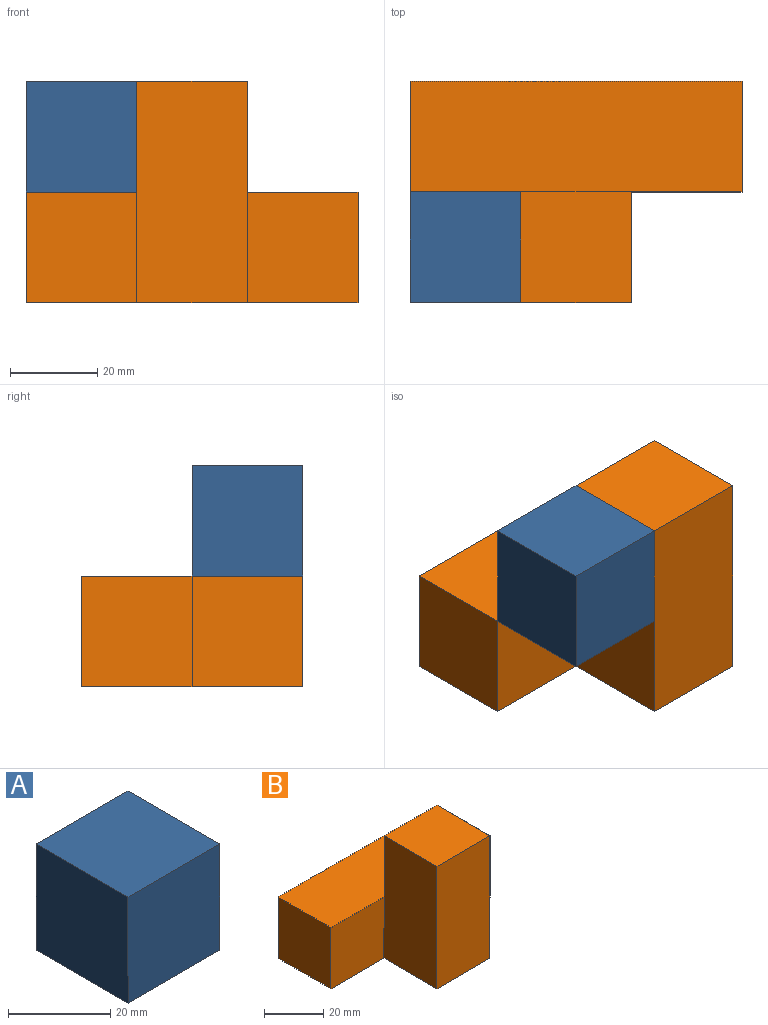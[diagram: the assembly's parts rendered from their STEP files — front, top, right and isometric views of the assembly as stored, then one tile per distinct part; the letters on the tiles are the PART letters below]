
ASSEMBLY  parts=2 mates=1
PART A: 6 faces, bbox 25.4x25.4x25.4 mm
  f0: plane 25.4x25.4mm, normal (-1,0,0), area 645.2mm2, adj f1,f3,f4,f5
  f1: plane 25.4x25.4mm, normal (0,0,-1), area 645.2mm2, adj f0,f2,f4,f5
  f2: plane 25.4x25.4mm, normal (1,0,0), area 645.2mm2, adj f1,f3,f4,f5
  f3: plane 25.4x25.4mm, normal (0,0,1), area 645.2mm2, adj f0,f2,f4,f5
  f4: plane 25.4x25.4mm, normal (0,-1,0), area 645.2mm2, adj f0,f1,f2,f3
  f5: plane 25.4x25.4mm, normal (0,1,0), area 645.2mm2, adj f0,f1,f2,f3
PART B: 12 faces, bbox 76.2x50.8x50.8 mm
  f0: plane 76.2x25.4mm, normal (0,0,1), area 1935.5mm2, adj f1,f2,f4,f5,f6,f10
  f1: plane 25.4x25.4mm, normal (0,-1,0), area 645.2mm2, adj f0,f3,f6,f7
  f2: plane 25.4x25.4mm, normal (0,-1,0), area 645.2mm2, adj f0,f3,f5,f8
  f3: plane 76.2x50.8mm, normal (0,0,-1), area 2580.6mm2, adj f1,f2,f4,f5,f6,f7,f8,f9
  f4: plane 76.2x25.4mm, normal (0,1,0), area 1935.5mm2, adj f0,f3,f5,f6
  f5: plane 25.4x25.4mm, normal (1,0,0), area 645.2mm2, adj f0,f2,f3,f4
  f6: plane 25.4x25.4mm, normal (-1,0,0), area 645.2mm2, adj f0,f1,f3,f4
  f7: plane 50.8x25.4mm, normal (-1,0,0), area 1290.3mm2, adj f1,f3,f9,f10,f11
  f8: plane 50.8x25.4mm, normal (1,0,0), area 1290.3mm2, adj f2,f3,f9,f10,f11
  f9: plane 50.8x25.4mm, normal (0,-1,0), area 1290.3mm2, adj f3,f7,f8,f11
  f10: plane 25.4x25.4mm, normal (0,1,0), area 645.2mm2, adj f0,f7,f8,f11
  f11: plane 25.4x25.4mm, normal (0,0,1), area 645.2mm2, adj f7,f8,f9,f10
PLACE A t=(-36.29,9.58,12.8)mm
PLACE B t=(-36.29,9.58,-12.6)mm
MATE revolute A.f3 <-> B.f11  axis (0,0,1) through (-10.89,-15.82,38.2)mm
